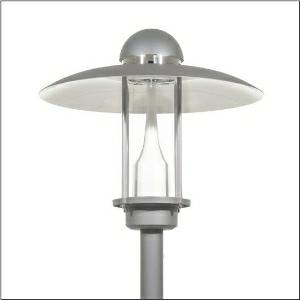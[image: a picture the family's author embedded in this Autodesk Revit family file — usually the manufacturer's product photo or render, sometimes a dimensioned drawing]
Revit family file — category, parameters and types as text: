
# Revit family: city-light_elegance_iq___p1_0a_5xa5265lf14h_79ad
name_source: partatom
category: Lighting Fixtures
units: mm (PartAtom-declared; Revit-internal decimal feet)

## family parameters
Cut with Voids When Loaded = No
Host = Face
Light Source = No
Part Type = Normal
Room Calculation Point = No
Round Connector Dimension = Use Diameter
Shared = No

## types (1)
- --- (1 x LED, 1440 lm, 10 W, 4000K)
    Apparent Load = 10 VA
    CIE Flux Codes = 32 62 91 97 100
    Color Rendering = 70
    Color Temperature = 4000K
    Default Elevation = 1800 mm
    Description = City-Light Elegance iQ, mast luminaire, Module 540 iQ-SR, primary light control with 3 zone facetted reflector, of plastic, silver coated, highly specular, structured, primary optical cover: cover, of PMMA, transparent, light distribution: P1.0a, light emission: direct distribution, primary light characteristic: strongly asymmetric, installation type: post-top, LED, High Power LED, rated luminous flux: 1.440lm, luminous efficacy: 144lm/W, light colour: 740, colour temperature: 4000K, control gear: ECG iQ, control: presetting dimming logarithmic, Street-Remote, Auto-Match, Temp-Guard, Lumen-Switch, Night-Set, Smart-Wire, Light-Fading, Desk-Remote (wireless, voltage-free reading and setting of iQ features in the workshop via application-optimized NFC function/RFID function), optimised constant luminous flux control (CLO 2.0), with terminal, 6-pole, max. 2.5mm², mains connection: 220..240V, AC, 50/60Hz, start of lifetime: 10W, end of lifetime: 10W, reduction: 5W, luminaire housing, upper part, of aluminium, coated, Siteco® metallic grey (DB 702S), diameter: 750mm, height: 675mm, spigot size: d x l = 76 x 70mm (post-top) | with reducer (optional accessory) 60 x 70mm, post-top mast mounting element, of diecast aluminium, coated, Siteco® metallic grey (DB 702S), Module 540 iQ-SR, traffic white (RAL 9016), equipment: standard, protection rating (complete): IP65, insulation class (complete): insulation class II (safety insulation), certification: CE, ENEC, VDE, packaging unit: 1 piece

Light Distribution: P1.0a
    Height = 675 mm
    Lamp = 1 x LED
    Lamp Light Flux = 1440 lm
    Lamp Power = 10 W
    Lamp count = 1
    Length = 750 mm
    Luminous efficacy = 144 lm/W
    Manufacturer = Siteco
    ModVariant = No
    Model = 5XA5265LF14H
    Number of Poles = 1
    OnlyDefault = Yes
    Power Factor = 1
    Product Name = City-Light Elegance iQ | P1.0a
    Product group = mast luminaire | pylon top
    ProductGroupID = 6100
    Protection Class = Protection class II
    Protection Degree = IP 65
    RLX_Detail_Level = 1
    RlxData = <blob elided: 106593 chars, md5=fd041f9d>
    Socket = socket
    Standby Power = 0 W
    System Light Flux = 1440 lm
    System Power = 10 W
    Type Comments = factory setting: luminous flux: 100 % | dim-lin: 254 | 401 mA
    Type Image = l_1006912.jpg
    URL = http://relux.com
    VarID = @adj_070939
    Voltage = 0 V
    Weight = 0.00 kg
    Width = 0 mm  [stored 0 ft]

note: [stored X ft] marks values corroborated as IEEE doubles in the binary element streams (Revit-internal decimal feet)

## geometry (parser evidence)
native form markers: Blend x4, Sweep x12
no freeform markers — native parametric forms only
